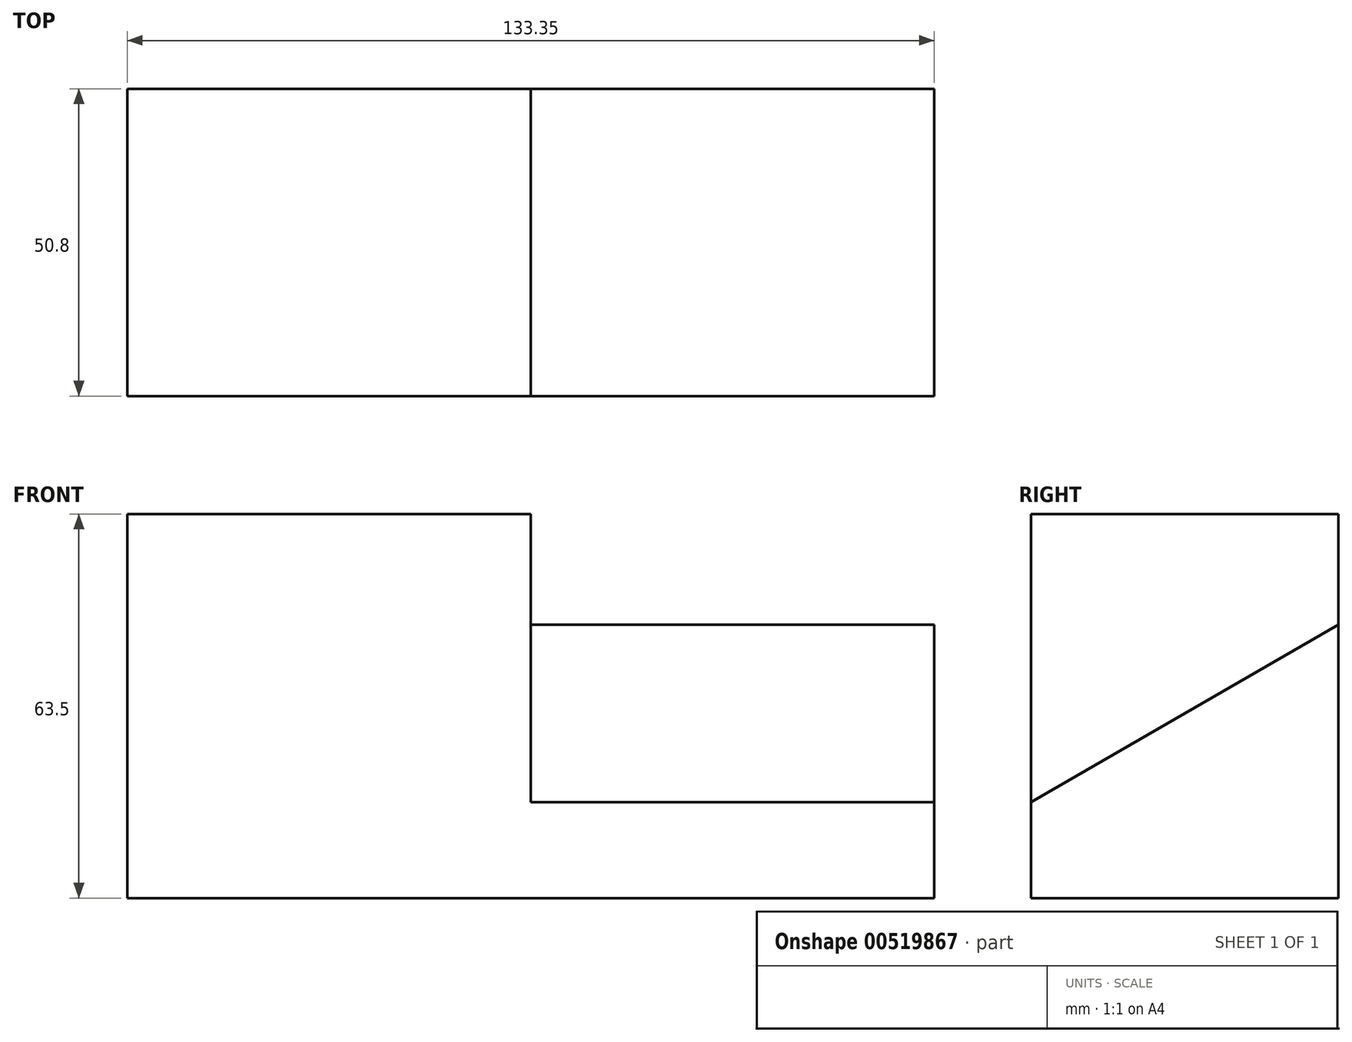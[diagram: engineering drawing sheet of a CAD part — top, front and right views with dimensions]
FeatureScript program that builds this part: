
annotation { "Feature Type Name" : "Feature", "Feature Type Description" : "" }
export const myFeature = defineFeature(function(context is Context, id is Id, definition is map)
    precondition{}
    {
        {
            var Q0;
            Q0=qCreatedBy(makeId("Front.planeOp"),FACE);
            var sketch = newSketch(context, id + "F0", { "sketchPlane" : qUnion([Q0])});
            skLineSegment(sketch, "E0.bottom", {"start": v(-69.94, 37.9) * mm, "end": v(63.4, 37.9) * mm});
            skLineSegment(sketch, "E0.top", {"start": v(-69.94, -25.6) * mm, "end": v(63.4, -25.6) * mm});
            skLineSegment(sketch, "E0.left", {"start": v(-69.94, 37.9) * mm, "end": v(-69.94, -25.6) * mm});
            skLineSegment(sketch, "E0.right", {"start": v(63.4, 37.9) * mm, "end": v(63.4, -25.6) * mm});
            skSolve(sketch);
        }
        {
            var Q0;
            Q0 = qSketchRegion(id + "F0", true);
            extrude(context, id + "F1", {"entities" : qUnion([Q0]), "depth" : 50.8 * mm, "offsetDistance" : 25.4 * mm});
        }
        {
            var Q0;
            Q0=makeQuery(id+"F1.opExtrude","SWEPT_FACE",FACE,{"disambiguationData":[OSD([sQuery(id+"F0.wireOp",EDGE,"E0.right")])]});
            var sketch = newSketch(context, id + "F2", { "sketchPlane" : qUnion([Q0])});
            skLineSegment(sketch, "E1", {"start": v(-50.8, -9.72) * mm, "end": v(0, 19.61) * mm});
            skSolve(sketch);
        }
        {
            var Q0;
            {var subQ0=sQuery(id+"F2.wireOp",EDGE,"E1");Q0=makeQuery(id+"F2.imprint","IMPRINT",FACE,{"disambiguationData":[TD([[makeQuery(id+"F2.imprint","IMPRINT",EDGE,{"derivedFrom":subQ0}),1.0]])]});}
            extrude(context, id + "F3", {"entities" : qUnion([Q0]), "operationType" : NewBodyOperationType.REMOVE, "oppositeDirection" : true, "depth" : 66.67 * mm, "offsetDistance" : 25.4 * mm});
        }
    });
